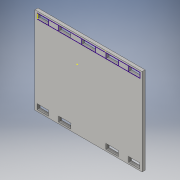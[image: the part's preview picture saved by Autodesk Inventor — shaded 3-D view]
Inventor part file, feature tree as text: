
AUTODESK INVENTOR PART (.ipt)
format: ipt  version: 2016 (Build 200138000, 138)  size: 144,384 bytes
history: native  units: in
note: dims shown in document units (in); Inventor stores cm internally (conversion verified against a paired STEP export)
features: sketch x2, extrude x1
ambient origin geometry x8: Origin, YZ Plane, XZ Plane, XY Plane, X Axis, Y Axis, Z Axis, Center Point
bodies: Solid1 (feature_tree)
feature tree (3):
  extrude  "Extrusion1"  [1 undecoded]
  sketch  "Sketch2"
  sketch  "Sketch1"  dims[d0=0.09in d1=0.0in]
note: 1 required parameter value undecoded (feature->parameter linkage not recoverable at this tier; creation-order binding heuristic only, values carry confidence <= 0.55)
